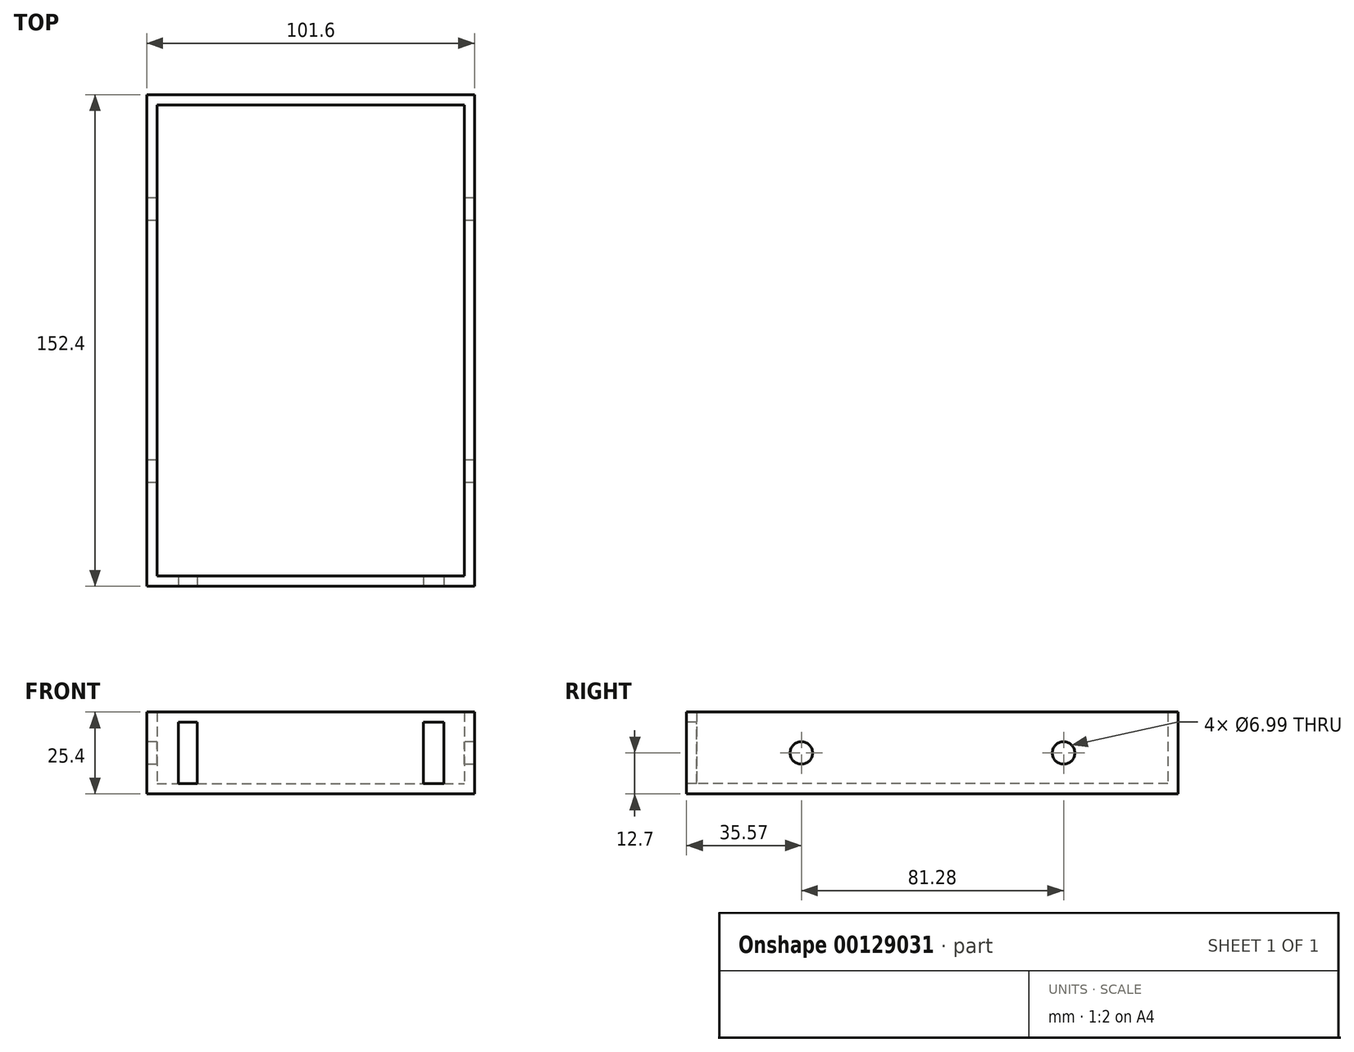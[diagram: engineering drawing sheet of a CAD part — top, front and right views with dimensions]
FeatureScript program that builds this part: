
annotation { "Feature Type Name" : "Feature", "Feature Type Description" : "" }
export const myFeature = defineFeature(function(context is Context, id is Id, definition is map)
    precondition{}
    {
        {
            var Q0;
            Q0=qCreatedBy(makeId("Top.planeOp"),FACE);
            var sketch = newSketch(context, id + "F0", { "sketchPlane" : qUnion([Q0])});
            skLineSegment(sketch, "E0.bottom", {"start": v(-50.8, 76.2) * mm, "end": v(50.8, 76.2) * mm});
            skLineSegment(sketch, "E0.top", {"start": v(-50.8, -76.2) * mm, "end": v(50.8, -76.2) * mm});
            skLineSegment(sketch, "E0.left", {"start": v(-50.8, 76.2) * mm, "end": v(-50.8, -76.2) * mm});
            skLineSegment(sketch, "E0.right", {"start": v(50.8, 76.2) * mm, "end": v(50.8, -76.2) * mm});
            skPoint(sketch, "E0.middle", {"position": v(0, 0) * mm});
            skLineSegment(sketch, "E1.bottom", {"start": v(-47.63, 73.03) * mm, "end": v(47.63, 73.03) * mm});
            skLineSegment(sketch, "E1.top", {"start": v(-47.63, -73.03) * mm, "end": v(47.62, -73.03) * mm});
            skLineSegment(sketch, "E1.left", {"start": v(-47.63, 73.03) * mm, "end": v(-47.63, -73.03) * mm});
            skLineSegment(sketch, "E1.right", {"start": v(47.63, 73.03) * mm, "end": v(47.62, -73.03) * mm});
            skSolve(sketch);
        }
        {
            var Q0;
            Q0=makeQuery(id+"F0.imprint","IMPRINT",FACE,{"disambiguationData":[TD([[makeQuery(id+"F0.imprint","IMPRINT",EDGE,{"derivedFrom":sQuery(id+"F0.wireOp",EDGE,"E1.bottom")}),-1.0]])]});
            extrude(context, id + "F1", {"entities" : qUnion([Q0]), "depth" : 3.17 * mm});
        }
        {
            var Q0;
            Q0=makeQuery(id+"F0.imprint","IMPRINT",FACE,{"disambiguationData":[TD([[makeQuery(id+"F0.imprint","IMPRINT",EDGE,{"derivedFrom":sQuery(id+"F0.wireOp",EDGE,"E0.bottom")}),-1.0]])]});
            extrude(context, id + "F2", {"entities" : qUnion([Q0]), "operationType" : NewBodyOperationType.ADD, "depth" : 25.4 * mm});
        }
        {
            var Q0;
            Q0=makeQuery(id+"F2.opExtrude","SWEPT_FACE",FACE,{"disambiguationData":[OSD([sQuery(id+"F0.wireOp",EDGE,"E0.left")])]});
            var sketch = newSketch(context, id + "F3", { "sketchPlane" : qUnion([Q0])});
            skLineSegment(sketch, "E2", {"start": v(-76.2, 25.4) * mm, "end": v(-101.61, 25.4) * mm});
            skLineSegment(sketch, "E3", {"start": v(76.2, 25.4) * mm, "end": v(101.59, 25.4) * mm});
            skLineSegment(sketch, "E4", {"start": v(-101.61, 25.4) * mm, "end": v(-101.61, 0) * mm});
            skLineSegment(sketch, "E5", {"start": v(101.59, 25.4) * mm, "end": v(101.59, 0) * mm});
            skLineSegment(sketch, "E6", {"start": v(-101.61, 12.7) * mm, "end": v(-40.65, 12.7) * mm});
            skCircle(sketch, "E7", {"center": v(-40.65, 12.7) * mm, "radius": 60.32 * mm});
            skLineSegment(sketch, "E8", {"start": v(101.59, 12.7) * mm, "end": v(40.63, 12.7) * mm});
            skPoint(sketch, "E8.endSnap0", {"position": v(76.2, 12.7) * mm});
            skArc(sketch, "E9", {"start": v(-32.7, 12.7) * mm, "mid": v(-40.65, 4.75) * mm, "end": v(-48.6, 12.7) * mm});
            skLineSegment(sketch, "E10", {"start": v(-48.6, 12.7) * mm, "end": v(-48.6, 25.4) * mm});
            skLineSegment(sketch, "E11", {"start": v(-32.7, 12.7) * mm, "end": v(-32.7, 25.4) * mm});
            skLineSegment(sketch, "E12", {"start": v(-32.7, 25.4) * mm, "end": v(-48.6, 25.4) * mm});
            skArc(sketch, "E13", {"start": v(32.68, 12.7) * mm, "mid": v(40.63, 4.75) * mm, "end": v(48.58, 12.7) * mm});
            skLineSegment(sketch, "E14", {"start": v(32.68, 12.7) * mm, "end": v(32.68, 25.4) * mm});
            skLineSegment(sketch, "E15", {"start": v(32.68, 25.4) * mm, "end": v(48.58, 25.4) * mm});
            skLineSegment(sketch, "E16", {"start": v(48.58, 25.4) * mm, "end": v(48.58, 12.7) * mm});
            skSolve(sketch);
        }
        {
            var Q0;
            Q0=sQuery(id+"F3.wireOp",VERTEX,"E9.center");
            var Q1;
            Q1=sQuery(id+"F3.wireOp",VERTEX,"E8.end");
            var Q2;
            Q2=makeQuery(id+"F1.opExtrude","SWEPT_BODY",BODY,{"disambiguationData":[OSD([sQuery(id+"F0.wireOp",EDGE,"E1.bottom"),sQuery(id+"F0.wireOp",EDGE,"E1.top"),sQuery(id+"F0.wireOp",EDGE,"E1.left"),sQuery(id+"F0.wireOp",EDGE,"E1.right")])]});
            hole(context, id + "F4", {"style" : HoleStyle.SIMPLE, "endStyle" : HoleEndStyle.THROUGH, "holeDiameter" : 7 * mm, "locations" : qUnion([Q0, Q1]), "scope" : qUnion([Q2]), "isTappedThrough" : true});
        }
        {
            var Q0;
            Q0=makeQuery(id+"F2.opExtrude","SWEPT_FACE",FACE,{"disambiguationData":[OSD([sQuery(id+"F0.wireOp",EDGE,"E0.top")])]});
            var sketch = newSketch(context, id + "F5", { "sketchPlane" : qUnion([Q0])});
            skLineSegment(sketch, "E17", {"start": v(0, 25.4) * mm, "end": v(-38.1, 25.4) * mm});
            skLineSegment(sketch, "E18", {"start": v(-38.1, 25.4) * mm, "end": v(-38.1, 0) * mm});
            skLineSegment(sketch, "E19", {"start": v(-38.1, 0) * mm, "end": v(0, 0) * mm});
            skLineSegment(sketch, "E20", {"start": v(0, 0) * mm, "end": v(38.1, 0) * mm});
            skLineSegment(sketch, "E21", {"start": v(38.1, 25.4) * mm, "end": v(0, 25.4) * mm});
            skLineSegment(sketch, "E22.bottom", {"start": v(-41.04, 22.23) * mm, "end": v(-35.15, 22.23) * mm});
            skLineSegment(sketch, "E22.top", {"start": v(-41.04, 3.17) * mm, "end": v(-35.15, 3.17) * mm});
            skLineSegment(sketch, "E22.left", {"start": v(-41.04, 22.23) * mm, "end": v(-41.04, 3.17) * mm});
            skLineSegment(sketch, "E22.right", {"start": v(-35.15, 22.23) * mm, "end": v(-35.15, 3.17) * mm});
            skPoint(sketch, "E22.middle", {"position": v(-38.1, 12.7) * mm});
            skLineSegment(sketch, "E23", {"start": v(38.1, 25.4) * mm, "end": v(38.1, 0) * mm});
            skLineSegment(sketch, "E24.bottom", {"start": v(34.92, 22.23) * mm, "end": v(41.28, 22.23) * mm});
            skLineSegment(sketch, "E24.top", {"start": v(34.92, 3.17) * mm, "end": v(41.28, 3.17) * mm});
            skLineSegment(sketch, "E24.left", {"start": v(34.92, 22.23) * mm, "end": v(34.92, 3.17) * mm});
            skLineSegment(sketch, "E24.right", {"start": v(41.28, 22.23) * mm, "end": v(41.28, 3.17) * mm});
            skPoint(sketch, "E24.middle", {"position": v(38.1, 12.7) * mm});
            skSolve(sketch);
        }
        {
            var Q0;
            {var subQ5=sQuery(id+"F5.wireOp",EDGE,"E22.left");Q0=makeQuery(id+"F5.imprint","IMPRINT",FACE,{"disambiguationData":[TD([[makeQuery(id+"F5.imprint","IMPRINT",EDGE,{"derivedFrom":subQ5}),1.0]])]});}
            var Q1;
            {var subQ5=sQuery(id+"F5.wireOp",EDGE,"E24.left");Q1=makeQuery(id+"F5.imprint","IMPRINT",FACE,{"disambiguationData":[TD([[makeQuery(id+"F5.imprint","IMPRINT",EDGE,{"derivedFrom":subQ5}),1.0]])]});}
            var Q2;
            {var subQ5=sQuery(id+"F5.wireOp",EDGE,"E24.right");Q2=makeQuery(id+"F5.imprint","IMPRINT",FACE,{"disambiguationData":[TD([[makeQuery(id+"F5.imprint","IMPRINT",EDGE,{"derivedFrom":subQ5}),-1.0]])]});}
            var Q3;
            {var subQ5=sQuery(id+"F5.wireOp",EDGE,"E22.right");Q3=makeQuery(id+"F5.imprint","IMPRINT",FACE,{"disambiguationData":[TD([[makeQuery(id+"F5.imprint","IMPRINT",EDGE,{"derivedFrom":subQ5}),-1.0]])]});}
            extrude(context, id + "F6", {"entities" : qUnion([Q0, Q1, Q2, Q3]), "operationType" : NewBodyOperationType.REMOVE, "oppositeDirection" : true, "depth" : 25.4 * mm});
        }
    });
